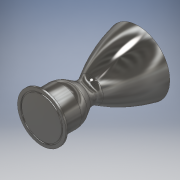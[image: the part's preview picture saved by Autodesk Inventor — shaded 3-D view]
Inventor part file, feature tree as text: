
AUTODESK INVENTOR PART (.ipt)
format: ipt  version: 2017 (Build 210142000, 142)  size: 251,392 bytes
history: native  units: in
note: dims shown in document units (in); Inventor stores cm internally (conversion verified against a paired STEP export)
features: fillet x4, other x2
ambient origin geometry x8: Origin, YZ Plane, XZ Plane, XY Plane, X Axis, Y Axis, Z Axis, Center Point
bodies: Body1 (feature_tree)
feature tree (6):
  other  "CD Nozzle"
  fillet  "Fillet14"  Radius=3.1496in
  fillet  "Fillet15"  [1 undecoded]
  fillet  "Fillet16"  Radius=1.7717in
  fillet  "Fillet17"  Radius=1.378in
  other  "CD Nozzle Sketch"
note: 1 required parameter value undecoded (feature->parameter linkage not recoverable at this tier; creation-order binding heuristic only, values carry confidence <= 0.55)
